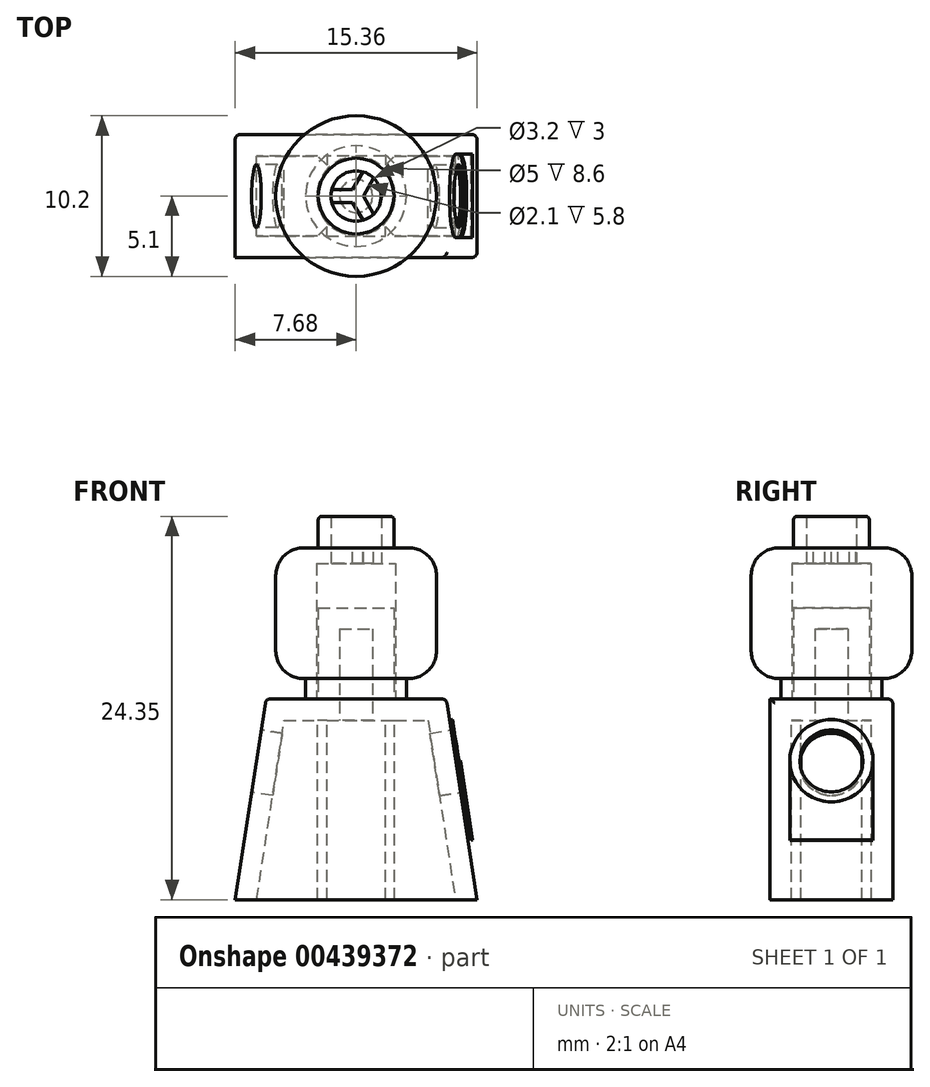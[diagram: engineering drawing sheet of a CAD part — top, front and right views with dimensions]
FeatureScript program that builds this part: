
annotation { "Feature Type Name" : "Feature", "Feature Type Description" : "" }
export const myFeature = defineFeature(function(context is Context, id is Id, definition is map)
    precondition{}
    {
        {
            var Q0;
            Q0=qCreatedBy(makeId("Front.planeOp"),FACE);
            var sketch = newSketch(context, id + "F0", { "sketchPlane" : qUnion([Q0])});
            skLineSegment(sketch, "E0", {"start": v(0, 0) * mm, "end": v(0, 11.6) * mm, "construction": true});
            skLineSegment(sketch, "E1", {"start": v(0, 0) * mm, "end": v(2.5, 0) * mm, "construction": true});
            skLineSegment(sketch, "E2", {"start": v(3.2, 0) * mm, "end": v(3.2, 1.3) * mm});
            skLineSegment(sketch, "E3", {"start": v(3.2, 1.3) * mm, "end": v(3.35, 1.3) * mm});
            skLineSegment(sketch, "E4", {"start": v(5.1, 3.05) * mm, "end": v(5.1, 7.85) * mm});
            skLineSegment(sketch, "E5", {"start": v(3.35, 9.6) * mm, "end": v(2.4, 9.6) * mm});
            skLineSegment(sketch, "E6", {"start": v(2.4, 9.6) * mm, "end": v(2.4, 11.4) * mm});
            skLineSegment(sketch, "E7", {"start": v(2.2, 11.6) * mm, "end": v(1.6, 11.6) * mm});
            skLineSegment(sketch, "E8", {"start": v(1.6, 11.6) * mm, "end": v(1.6, 9.6) * mm});
            skLineSegment(sketch, "E9", {"start": v(1.6, 9.6) * mm, "end": v(0, 9.6) * mm});
            skLineSegment(sketch, "E10", {"start": v(0, 9.6) * mm, "end": v(0, 8.6) * mm});
            skLineSegment(sketch, "E11", {"start": v(0, 8.6) * mm, "end": v(2.5, 8.6) * mm});
            skLineSegment(sketch, "E12", {"start": v(2.5, 8.6) * mm, "end": v(2.5, 0) * mm});
            skPoint(sketch, "E13.visualSharp", {"position": v(5.1, 9.6) * mm});
            skArc(sketch, "E13.filletArc", {"start": v(5.1, 7.85) * mm, "mid": v(4.59, 9.09) * mm, "end": v(3.35, 9.6) * mm});
            skPoint(sketch, "E14.visualSharp", {"position": v(5.1, 1.3) * mm});
            skArc(sketch, "E14.filletArc", {"start": v(3.35, 1.3) * mm, "mid": v(4.59, 1.81) * mm, "end": v(5.1, 3.05) * mm});
            skPoint(sketch, "E15.visualSharp", {"position": v(2.4, 11.6) * mm});
            skArc(sketch, "E15.filletArc", {"start": v(2.4, 11.4) * mm, "mid": v(2.34, 11.54) * mm, "end": v(2.2, 11.6) * mm});
            skLineSegment(sketch, "E16", {"start": v(2.5, 0) * mm, "end": v(3.2, 0) * mm});
            skSolve(sketch);
        }
        {
            var Q0;
            Q0=makeQuery(id+"F0.imprint","IMPRINT",FACE,{"disambiguationData":[TD([[makeQuery(id+"F0.imprint","IMPRINT",EDGE,{"derivedFrom":sQuery(id+"F0.wireOp",EDGE,"E2")}),1.0]])]});
            var Q1;
            Q1=sQuery(id+"F0.wireOp",EDGE,"E0");
            revolve(context, id + "F1", {"entities" : qUnion([Q0]), "axis" : qUnion([Q1]), "revolveType" : RevolveType.FULL});
        }
        {
            var Q0;
            Q0=makeQuery(id+"F1.opRevolve","SWEPT_FACE",FACE,{"disambiguationData":[OSD([sQuery(id+"F0.wireOp",EDGE,"E9")])]});
            var sketch = newSketch(context, id + "F2", { "sketchPlane" : qUnion([Q0])});
            skCircle(sketch, "E17", {"center": v(0, 0) * mm, "radius": 0.4 * mm});
            skLineSegment(sketch, "E18", {"start": v(0, 0) * mm, "end": v(0, -0.4) * mm, "construction": true});
            skLineSegment(sketch, "E19", {"start": v(0, 0) * mm, "end": v(0, 0.4) * mm, "construction": true});
            skLineSegment(sketch, "E20", {"start": v(0, -0.4) * mm, "end": v(-1.55, -0.4) * mm});
            skLineSegment(sketch, "E21", {"start": v(0, 0.4) * mm, "end": v(-1.55, 0.4) * mm});
            skLineSegment(sketch, "E22.1.1", {"start": v(0.35, 0.2) * mm, "end": v(1.12, -1.14) * mm});
            skLineSegment(sketch, "E22.1.2", {"start": v(-0.35, -0.2) * mm, "end": v(0.43, -1.54) * mm});
            skLineSegment(sketch, "E22.2.1", {"start": v(-0.35, 0.2) * mm, "end": v(0.43, 1.54) * mm});
            skLineSegment(sketch, "E22.2.2", {"start": v(0.35, -0.2) * mm, "end": v(1.12, 1.14) * mm});
            skSolve(sketch);
        }
        {
            var Q0;
            {var subQ0=sQuery(id+"F2.wireOp",EDGE,"E21");var subQ3=sQuery(id+"F2.wireOp",EDGE,"E22.2.1");var subQ4=makeQuery(id+"F2.imprint","INTERSECT",VERTEX,{"derivedFrom":[subQ0,subQ3]});Q0=makeQuery(id+"F2.imprint","IMPRINT",FACE,{"disambiguationData":[TD([[makeQuery(id+"F2.imprint","IMPRINT",EDGE,{"disambiguationData":[TD([[subQ4,-1.0]])],"derivedFrom":subQ0}),-1.0]])]});}
            var Q1;
            {var subQ0=sQuery(id+"F2.wireOp",EDGE,"E22.1.1");var subQ3=sQuery(id+"F2.wireOp",EDGE,"E22.2.2");var subQ4=makeQuery(id+"F2.imprint","INTERSECT",VERTEX,{"derivedFrom":[subQ0,subQ3]});Q1=makeQuery(id+"F2.imprint","IMPRINT",FACE,{"disambiguationData":[TD([[makeQuery(id+"F2.imprint","IMPRINT",EDGE,{"disambiguationData":[TD([[subQ4,-1.0]])],"derivedFrom":subQ0}),1.0]])]});}
            var Q2;
            {var subQ0=sQuery(id+"F2.wireOp",EDGE,"E20");var subQ3=sQuery(id+"F2.wireOp",EDGE,"E22.1.2");var subQ4=makeQuery(id+"F2.imprint","INTERSECT",VERTEX,{"derivedFrom":[subQ0,subQ3]});Q2=makeQuery(id+"F2.imprint","IMPRINT",FACE,{"disambiguationData":[TD([[makeQuery(id+"F2.imprint","IMPRINT",EDGE,{"disambiguationData":[TD([[subQ4,-1.0]])],"derivedFrom":subQ0}),1.0]])]});}
            extrude(context, id + "F3", {"entities" : qUnion([Q0, Q1, Q2]), "operationType" : NewBodyOperationType.REMOVE, "oppositeDirection" : true, "depth" : 25 * mm});
        }
        {
            var Q0;
            Q0=makeQuery(id+"F1.opRevolve","SWEPT_FACE",FACE,{"disambiguationData":[OSD([sQuery(id+"F0.wireOp",EDGE,"E16")])]});
            var sketch = newSketch(context, id + "F4", { "sketchPlane" : qUnion([Q0])});
            skCircle(sketch, "E23", {"center": v(0, 0) * mm, "radius": 2.4 * mm});
            skSolve(sketch);
        }
        {
            var Q0;
            Q0=makeQuery(id+"F4.imprint","IMPRINT",FACE,{"disambiguationData":[TD([[makeQuery(id+"F4.imprint","IMPRINT",EDGE,{"derivedFrom":sQuery(id+"F4.wireOp",EDGE,"E23")}),1.0]])]});
            extrude(context, id + "F5", {"entities" : qUnion([Q0]), "oppositeDirection" : true, "depth" : 5.8 * mm});
        }
        {
            var Q0;
            Q0=qCreatedBy(makeId("Front.planeOp"),FACE);
            var sketch = newSketch(context, id + "F6", { "sketchPlane" : qUnion([Q0])});
            skLineSegment(sketch, "E24", {"start": v(0, 0) * mm, "end": v(0, -12.75) * mm, "construction": true});
            skLineSegment(sketch, "E25", {"start": v(-5.72, 0) * mm, "end": v(5.72, 0) * mm});
            skLineSegment(sketch, "E26", {"start": v(5.73, 0) * mm, "end": v(7.68, -12.75) * mm});
            skLineSegment(sketch, "E27", {"start": v(7.68, -12.75) * mm, "end": v(-7.67, -12.75) * mm});
            skLineSegment(sketch, "E28", {"start": v(-7.67, -12.75) * mm, "end": v(-5.73, 0) * mm});
            skSolve(sketch);
        }
        {
            var Q0;
            Q0 = qSketchRegion(id + "F6", true);
            extrude(context, id + "F7", {"entities" : qUnion([Q0]), "operationType" : NewBodyOperationType.ADD, "endBound" : BoundingType.SYMMETRIC, "depth" : 7.8 * mm});
        }
        {
            var Q0;
            Q0=makeQuery(id+"F7.opExtrude","SWEPT_FACE",FACE,{"disambiguationData":[OSD([sQuery(id+"F6.wireOp",EDGE,"E27")])]});
            shell(context, id + "F8", {"entities" : qUnion([Q0]), "thickness" : 1.35 * mm});
        }
        {
            var Q0;
            Q0=makeQuery(id+"F8.opShell","OFFSET_FACE",FACE,{"disambiguationData":[OSD([sQuery(id+"F6.wireOp",EDGE,"E25")])]});
            var sketch = newSketch(context, id + "F9", { "sketchPlane" : qUnion([Q0])});
            skLineSegment(sketch, "E29", {"start": v(0, 2.55) * mm, "end": v(0, -2.55) * mm, "construction": true});
            skLineSegment(sketch, "E30", {"start": v(-1.86, 2.55) * mm, "end": v(-1.86, 1.95) * mm});
            skLineSegment(sketch, "E31", {"start": v(-1.86, 1.95) * mm, "end": v(-2.46, 2.55) * mm});
            skLineSegment(sketch, "E32", {"start": v(-4.57, 0) * mm, "end": v(4.57, 0) * mm, "construction": true});
            skLineSegment(sketch, "E33.MirrorCS", {"start": v(1.86, 1.95) * mm, "end": v(2.46, 2.55) * mm});
            skLineSegment(sketch, "E34.MirrorCS", {"start": v(1.86, 2.55) * mm, "end": v(1.86, 1.95) * mm});
            skLineSegment(sketch, "E35.MirrorCS", {"start": v(4.57, 0) * mm, "end": v(-4.57, 0) * mm, "construction": true});
            skLineSegment(sketch, "E36.MirrorCS", {"start": v(-1.86, -1.95) * mm, "end": v(-2.46, -2.55) * mm});
            skLineSegment(sketch, "E37.MirrorCS", {"start": v(1.86, -1.95) * mm, "end": v(2.46, -2.55) * mm});
            skLineSegment(sketch, "E38.MirrorCS", {"start": v(1.86, -2.55) * mm, "end": v(1.86, -1.95) * mm});
            skLineSegment(sketch, "E39.MirrorCS", {"start": v(-1.86, -2.55) * mm, "end": v(-1.86, -1.95) * mm});
            skSolve(sketch);
        }
        {
            var Q0;
            {var subQ0=sQuery(id+"F9.wireOp",EDGE,"E30");Q0=makeQuery(id+"F9.imprint","IMPRINT",FACE,{"disambiguationData":[TD([[makeQuery(id+"F9.imprint","IMPRINT",EDGE,{"derivedFrom":subQ0}),-1.0]])]});}
            var Q1;
            {var subQ0=sQuery(id+"F9.wireOp",EDGE,"E33.MirrorCS");Q1=makeQuery(id+"F9.imprint","IMPRINT",FACE,{"disambiguationData":[TD([[makeQuery(id+"F9.imprint","IMPRINT",EDGE,{"derivedFrom":subQ0}),1.0]])]});}
            var Q2;
            {var subQ0=sQuery(id+"F9.wireOp",EDGE,"E36.MirrorCS");Q2=makeQuery(id+"F9.imprint","IMPRINT",FACE,{"disambiguationData":[TD([[makeQuery(id+"F9.imprint","IMPRINT",EDGE,{"derivedFrom":subQ0}),1.0]])]});}
            var Q3;
            {var subQ0=sQuery(id+"F9.wireOp",EDGE,"E37.MirrorCS");Q3=makeQuery(id+"F9.imprint","IMPRINT",FACE,{"disambiguationData":[TD([[makeQuery(id+"F9.imprint","IMPRINT",EDGE,{"derivedFrom":subQ0}),-1.0]])]});}
            var Q4;
            Q4=makeQuery(id+"F7.opExtrude","SWEPT_FACE",FACE,{"disambiguationData":[OSD([sQuery(id+"F6.wireOp",EDGE,"E27")])]});
            extrude(context, id + "F10", {"entities" : qUnion([Q0, Q1, Q2, Q3]), "operationType" : NewBodyOperationType.ADD, "endBound" : BoundingType.UP_TO_SURFACE, "endBoundEntityFace" : qUnion([Q4]), "depth" : 25 * mm});
        }
        {
            var Q0;
            Q0=makeQuery(id+"F7.opExtrude","SWEPT_FACE",FACE,{"disambiguationData":[OSD([sQuery(id+"F6.wireOp",EDGE,"E26")])]});
            var sketch = newSketch(context, id + "F11", { "sketchPlane" : qUnion([Q0])});
            skCircle(sketch, "E40", {"center": v(0, -4.87) * mm, "radius": 2 * mm});
            skPoint(sketch, "E40.centerSnap0", {"position": v(0, -0.87) * mm});
            skSolve(sketch);
        }
        {
            var Q0;
            Q0=makeQuery(id+"F7.opExtrude","SWEPT_FACE",FACE,{"disambiguationData":[OSD([sQuery(id+"F6.wireOp",EDGE,"E28")])]});
            var sketch = newSketch(context, id + "F12", { "sketchPlane" : qUnion([Q0])});
            skCircle(sketch, "E41", {"center": v(0, -4.87) * mm, "radius": 2 * mm});
            skPoint(sketch, "E41.centerSnap0", {"position": v(0, -0.87) * mm});
            skSolve(sketch);
        }
        {
            var Q0;
            Q0=makeQuery(id+"F12.imprint","IMPRINT",FACE,{"disambiguationData":[TD([[makeQuery(id+"F12.imprint","IMPRINT",EDGE,{"derivedFrom":sQuery(id+"F12.wireOp",EDGE,"E41")}),1.0]])]});
            extrude(context, id + "F13", {"entities" : qUnion([Q0]), "operationType" : NewBodyOperationType.REMOVE, "oppositeDirection" : true, "depth" : 1.35 * mm});
        }
        {
            var Q0;
            Q0=makeQuery(id+"F11.imprint","IMPRINT",FACE,{"disambiguationData":[TD([[makeQuery(id+"F11.imprint","IMPRINT",EDGE,{"derivedFrom":sQuery(id+"F11.wireOp",EDGE,"E40")}),1.0]])]});
            extrude(context, id + "F14", {"entities" : qUnion([Q0]), "operationType" : NewBodyOperationType.REMOVE, "oppositeDirection" : true, "depth" : 1.35 * mm});
        }
        {
            var Q0;
            Q0=makeQuery(id+"F7.opExtrude","CAP_EDGE",EDGE,{"disambiguationData":[OSD([sQuery(id+"F6.wireOp",EDGE,"E28")])],"isStart":true});
            var Q1;
            Q1=makeQuery(id+"F7.opExtrude","CAP_EDGE",EDGE,{"disambiguationData":[OSD([sQuery(id+"F6.wireOp",EDGE,"E25")])],"isStart":true});
            var Q2;
            Q2=makeQuery(id+"F7.opExtrude","SWEPT_EDGE",EDGE,{"disambiguationData":[OSD([sQuery(id+"F6.wireOp",EDGE,"E25"),sQuery(id+"F6.wireOp",EDGE,"E28")])]});
            var Q3;
            Q3=makeQuery(id+"F7.opExtrude","CAP_EDGE",EDGE,{"disambiguationData":[OSD([sQuery(id+"F6.wireOp",EDGE,"E26")])],"isStart":true});
            var Q4;
            Q4=makeQuery(id+"F7.opExtrude","SWEPT_EDGE",EDGE,{"disambiguationData":[OSD([sQuery(id+"F6.wireOp",EDGE,"E25"),sQuery(id+"F6.wireOp",EDGE,"E26")])]});
            var Q5;
            Q5=makeQuery(id+"F7.opExtrude","CAP_EDGE",EDGE,{"disambiguationData":[OSD([sQuery(id+"F6.wireOp",EDGE,"E26")])],"isStart":false});
            fillet(context, id + "F15", {"entities" : qUnion([Q0, Q1, Q2, Q3, Q4, Q5]), "radius" : 0.3 * mm, "tangentPropagation" : true, "allowEdgeOverflow" : false});
        }
        {
            var Q0;
            Q0=makeQuery(id+"F7.opExtrude","SWEPT_FACE",FACE,{"disambiguationData":[OSD([sQuery(id+"F6.wireOp",EDGE,"E26")])]});
            var sketch = newSketch(context, id + "F16", { "sketchPlane" : qUnion([Q0])});
            skCircle(sketch, "E42", {"center": v(0, -4.87) * mm, "radius": 2.65 * mm});
            skSolve(sketch);
        }
        {
            var Q0;
            Q0=makeQuery(id+"F16.imprint","IMPRINT",FACE,{"disambiguationData":[TD([[makeQuery(id+"F16.imprint","IMPRINT",EDGE,{"derivedFrom":makeQuery(id+"F14.boolean.opBoolean","COPY",EDGE,{"derivedFrom":makeQuery(id+"F14.opExtrude","CAP_EDGE",EDGE,{"disambiguationData":[OSD([sQuery(id+"F11.wireOp",EDGE,"E40")])],"isStart":true})})}),1.0]])]});
            var Q1;
            Q1=makeQuery(id+"F16.imprint","IMPRINT",FACE,{"disambiguationData":[TD([[makeQuery(id+"F16.imprint","IMPRINT",EDGE,{"derivedFrom":sQuery(id+"F16.wireOp",EDGE,"E42")}),1.0]])]});
            extrude(context, id + "F17", {"entities" : qUnion([Q0, Q1]), "depth" : 0.2 * mm, "offsetDistance" : 25 * mm});
        }
        {
            var Q0;
            Q0=makeQuery(id+"F17.opExtrude","CAP_FACE",FACE,{"disambiguationData":[OSD([sQuery(id+"F16.wireOp",EDGE,"E42")])],"isStart":false});
            var sketch = newSketch(context, id + "F18", { "sketchPlane" : qUnion([Q0])});
            skCircle(sketch, "E43", {"center": v(0, -4.87) * mm, "radius": 2.65 * mm});
            skLineSegment(sketch, "E44", {"start": v(0, -4.87) * mm, "end": v(-2.65, -4.87) * mm});
            skLineSegment(sketch, "E45", {"start": v(-2.65, -4.87) * mm, "end": v(2.65, -4.87) * mm});
            skLineSegment(sketch, "E46", {"start": v(2.65, -4.87) * mm, "end": v(2.65, -9.97) * mm});
            skLineSegment(sketch, "E47", {"start": v(-2.65, -4.87) * mm, "end": v(-2.65, -9.97) * mm});
            skLineSegment(sketch, "E48", {"start": v(-2.65, -9.97) * mm, "end": v(2.65, -9.97) * mm});
            skLineSegment(sketch, "E49", {"start": v(2.65, -9.97) * mm, "end": v(-1.29, -14.5) * mm});
            skLineSegment(sketch, "E50", {"start": v(-1.29, -14.5) * mm, "end": v(-4.3, -11.87) * mm});
            skLineSegment(sketch, "E51", {"start": v(-4.3, -11.87) * mm, "end": v(-2.65, -9.97) * mm});
            skSolve(sketch);
        }
        {
            var Q0;
            {var subQ0=sQuery(id+"F18.wireOp",EDGE,"E45");var subQ4=makeQuery(id+"F18.imprint","IMPRINT",VERTEX,{"derivedFrom":subQ0});Q0=makeQuery(id+"F18.imprint","IMPRINT",FACE,{"disambiguationData":[TD([[makeQuery(id+"F18.imprint","IMPRINT",EDGE,{"disambiguationData":[TD([[subQ4,1.0]])],"derivedFrom":subQ0}),-1.0]])]});}
            var Q1;
            {var subQ3=sQuery(id+"F18.wireOp",EDGE,"E46");Q1=makeQuery(id+"F18.imprint","IMPRINT",FACE,{"disambiguationData":[TD([[makeQuery(id+"F18.imprint","IMPRINT",EDGE,{"derivedFrom":subQ3}),-1.0]])]});}
            extrude(context, id + "F19", {"entities" : qUnion([Q0, Q1]), "operationType" : NewBodyOperationType.ADD, "depth" : 0.1 * mm, "offsetDistance" : 25 * mm});
        }
    });
